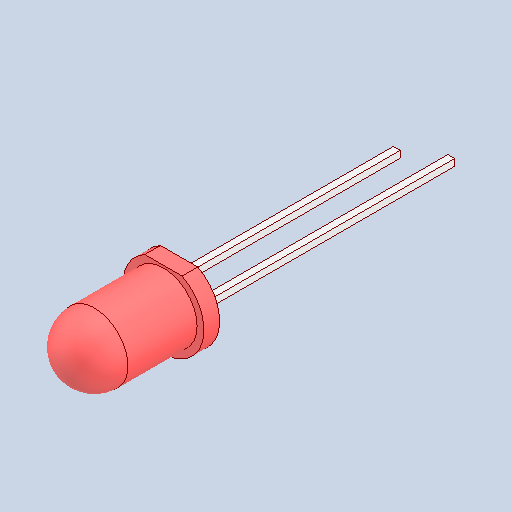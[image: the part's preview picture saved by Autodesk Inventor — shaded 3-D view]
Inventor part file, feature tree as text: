
AUTODESK INVENTOR PART (.ipt)
format: ipt  version: 2023 (Build 270158000, 158)  size: 278,528 bytes
history: mixed  units: in
note: dims shown in document units (in); Inventor stores cm internally (conversion verified against a paired STEP export)
features: extrude x1, imported_body x1
ambient origin geometry x8: Origin, YZ Plane, XZ Plane, XY Plane, X Axis, Y Axis, Z Axis, Center Point
bodies: Solid1 (imported_parasolid)
feature tree (2):
  extrude  "Extrude5"  [1 undecoded]
  imported_body  NMx_Import_Brep_tag  [imported B-rep: ~16 faces, bbox_mm=[4.94, 4.15, 26.23]]
note: 1 required parameter value undecoded (feature->parameter linkage not recoverable at this tier; creation-order binding heuristic only, values carry confidence <= 0.55)
